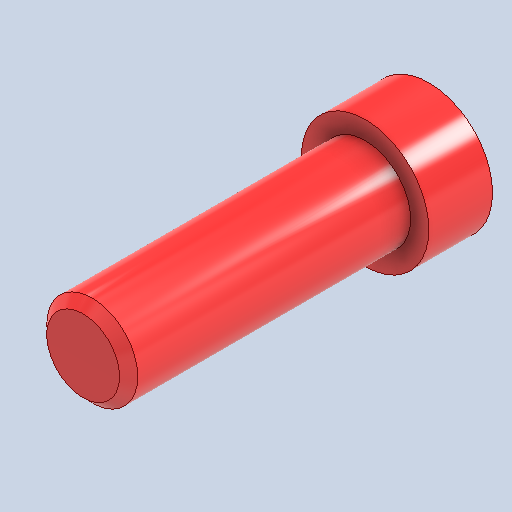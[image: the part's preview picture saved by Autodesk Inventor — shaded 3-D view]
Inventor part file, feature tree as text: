
AUTODESK INVENTOR PART (.ipt)
format: ipt  version: 2022 (Build 260153000, 153)  size: 135,168 bytes
history: native  units: in
note: dims shown in document units (in); Inventor stores cm internally (conversion verified against a paired STEP export)
features: extrude x2, sketch x2, chamfer x1
ambient origin geometry x8: Origin, YZ Plane, XZ Plane, XY Plane, X Axis, Y Axis, Z Axis, Center Point
bodies: Solid1 (feature_tree)
feature tree (5):
  extrude  "Extrusion1"  Depth=0.2756in TaperAngle=0.0deg
  extrude  "Extrusion2"  Depth=1.2205in TaperAngle=0.0deg
  chamfer  "Chamfer1"  Distance=0.0394in Angle=45.0deg
  sketch  "Sketch1"  dims[d0=0.5512in d1=0.2756in d2=0.0in]
  sketch  "Sketch2"  dims[d3=0.3937in d4=1.2205in d5=0.0in d6=0.0394in d7=0.0787in d8=45.0deg]
